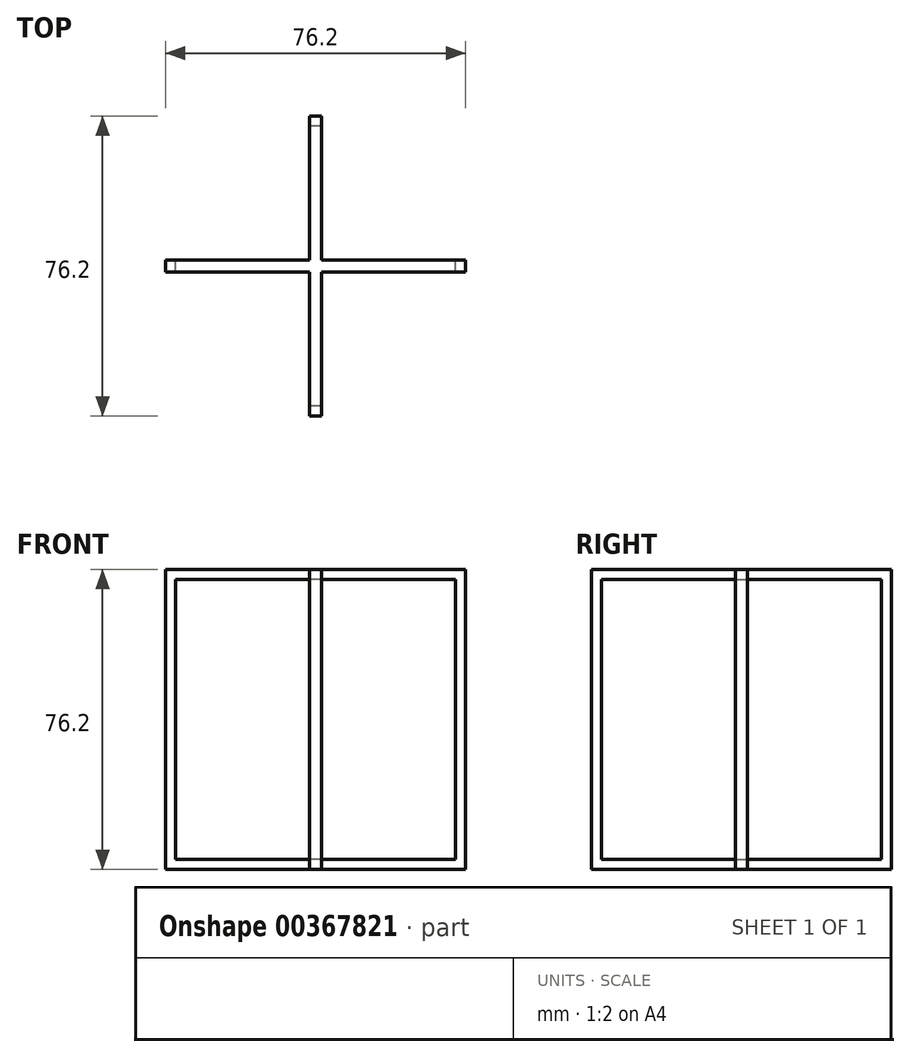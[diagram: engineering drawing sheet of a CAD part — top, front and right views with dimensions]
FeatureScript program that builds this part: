
annotation { "Feature Type Name" : "Feature", "Feature Type Description" : "" }
export const myFeature = defineFeature(function(context is Context, id is Id, definition is map)
    precondition{}
    {
        {
            assignVariable(context, id + "F0", {"name" : "Lenght", "anyValue" : 3});
        }
        {
            assignVariable(context, id + "F1", {"name" : "Width", "anyValue" : 3});
        }
        {
            var Q0;
            Q0=qCreatedBy(makeId("Front.planeOp"),FACE);
            var sketch = newSketch(context, id + "F2", { "sketchPlane" : qUnion([Q0])});
            skPoint(sketch, "E0.0", {"position": v(0, 0) * mm});
            skLineSegment(sketch, "E1.bottom", {"start": v(38.1, -38.1) * mm, "end": v(-38.1, -38.1) * mm});
            skLineSegment(sketch, "E1.top", {"start": v(38.1, 38.1) * mm, "end": v(-38.1, 38.1) * mm});
            skLineSegment(sketch, "E1.left", {"start": v(38.1, -38.1) * mm, "end": v(38.1, 38.1) * mm});
            skLineSegment(sketch, "E1.right", {"start": v(-38.1, -38.1) * mm, "end": v(-38.1, 38.1) * mm});
            skLineSegment(sketch, "E2.bottom", {"start": v(35.56, -35.56) * mm, "end": v(-35.56, -35.56) * mm});
            skLineSegment(sketch, "E2.top", {"start": v(35.56, 35.56) * mm, "end": v(-35.56, 35.56) * mm});
            skLineSegment(sketch, "E2.left", {"start": v(35.56, -35.56) * mm, "end": v(35.56, 35.56) * mm});
            skLineSegment(sketch, "E2.right", {"start": v(-35.56, -35.56) * mm, "end": v(-35.56, 35.56) * mm});
            skSolve(sketch);
        }
        {
            var Q0;
            Q0=qCreatedBy(makeId("Right.planeOp"),FACE);
            var sketch = newSketch(context, id + "F3", { "sketchPlane" : qUnion([Q0])});
            skLineSegment(sketch, "E3.bottom", {"start": v(-38.1, -38.1) * mm, "end": v(38.1, -38.1) * mm});
            skLineSegment(sketch, "E3.top", {"start": v(-38.1, 38.1) * mm, "end": v(38.1, 38.1) * mm});
            skLineSegment(sketch, "E3.left", {"start": v(-38.1, -38.1) * mm, "end": v(-38.1, 38.1) * mm});
            skLineSegment(sketch, "E3.right", {"start": v(38.1, -38.1) * mm, "end": v(38.1, 38.1) * mm});
            skPoint(sketch, "E3.middle", {"position": v(0, 0) * mm});
            skLineSegment(sketch, "E4.bottom", {"start": v(35.56, 35.56) * mm, "end": v(-35.56, 35.56) * mm});
            skLineSegment(sketch, "E4.top", {"start": v(35.56, -35.56) * mm, "end": v(-35.56, -35.56) * mm});
            skLineSegment(sketch, "E4.left", {"start": v(35.56, 35.56) * mm, "end": v(35.56, -35.56) * mm});
            skLineSegment(sketch, "E4.right", {"start": v(-35.56, 35.56) * mm, "end": v(-35.56, -35.56) * mm});
            skSolve(sketch);
        }
        {
            var Q0;
            Q0=makeQuery(id+"F3.imprint","IMPRINT",FACE,{"disambiguationData":[TD([[makeQuery(id+"F3.imprint","IMPRINT",EDGE,{"derivedFrom":sQuery(id+"F3.wireOp",EDGE,"E3.bottom")}),1.0]])]});
            extrude(context, id + "F4", {"entities" : qUnion([Q0]), "endBound" : BoundingType.SYMMETRIC, "depth" : (getVariable(context, 'Lenght')) * mm});
        }
        {
            var Q0;
            Q0=makeQuery(id+"F2.imprint","IMPRINT",FACE,{"disambiguationData":[TD([[makeQuery(id+"F2.imprint","IMPRINT",EDGE,{"derivedFrom":sQuery(id+"F2.wireOp",EDGE,"E1.bottom")}),-1.0]])]});
            extrude(context, id + "F5", {"entities" : qUnion([Q0]), "operationType" : NewBodyOperationType.ADD, "endBound" : BoundingType.SYMMETRIC, "depth" : (getVariable(context, 'Width')) * mm});
        }
    });
